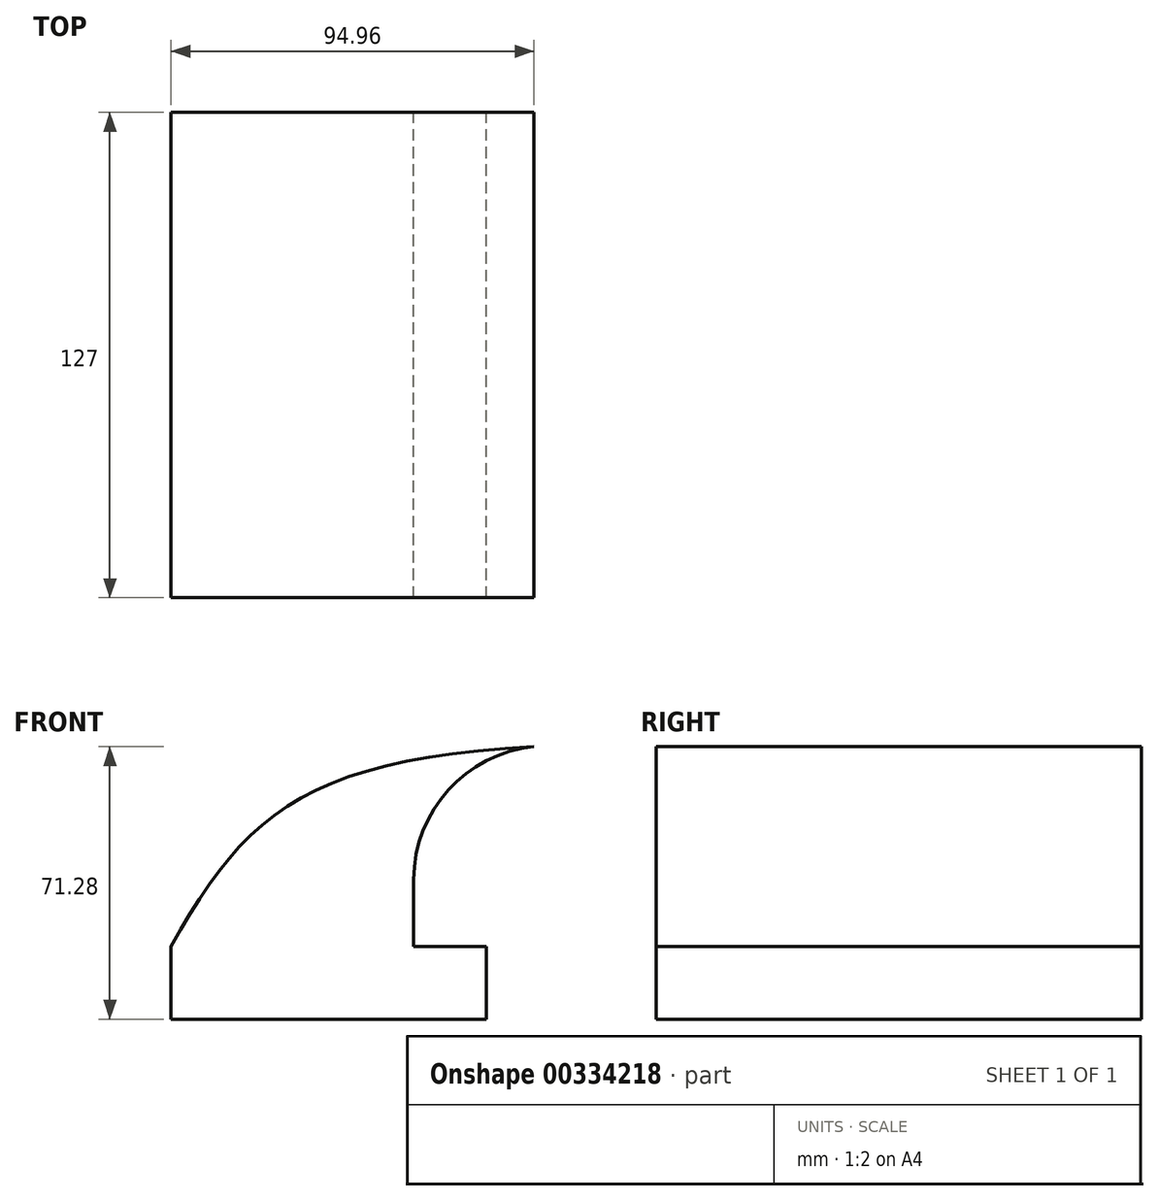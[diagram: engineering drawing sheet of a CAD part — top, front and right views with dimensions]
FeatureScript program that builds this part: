
annotation { "Feature Type Name" : "Feature", "Feature Type Description" : "" }
export const myFeature = defineFeature(function(context is Context, id is Id, definition is map)
    precondition{}
    {
        {
            var Q0;
            Q0=qCreatedBy(makeId("Front.planeOp"),FACE);
            var sketch = newSketch(context, id + "F0", { "sketchPlane" : qUnion([Q0])});
            skLineSegment(sketch, "E0.bottom", {"start": v(-41.28, 9.52) * mm, "end": v(41.28, 9.53) * mm});
            skLineSegment(sketch, "E0.top", {"start": v(-41.28, -9.52) * mm, "end": v(41.28, -9.52) * mm});
            skLineSegment(sketch, "E0.left", {"start": v(-41.28, 9.52) * mm, "end": v(-41.27, -9.53) * mm});
            skLineSegment(sketch, "E0.right", {"start": v(41.28, 9.53) * mm, "end": v(41.28, -9.52) * mm});
            skPoint(sketch, "E0.middle", {"position": v(0, 0) * mm});
            skLineSegment(sketch, "E1.bottom", {"start": v(130.2, 38.1) * mm, "end": v(79.4, 38.1) * mm});
            skLineSegment(sketch, "E1.top", {"start": v(130.2, 66.68) * mm, "end": v(79.4, 66.68) * mm});
            skLineSegment(sketch, "E1.left", {"start": v(130.2, 38.1) * mm, "end": v(130.2, 66.68) * mm});
            skLineSegment(sketch, "E1.right", {"start": v(79.4, 38.1) * mm, "end": v(79.4, 66.68) * mm});
            skPoint(sketch, "E1.middle", {"position": v(104.8, 52.39) * mm});
            skLineSegment(sketch, "E2", {"start": v(41.27, 9.53) * mm, "end": v(41.27, 27) * mm});
            skArc(sketch, "E3", {"start": v(41.27, 27) * mm, "mid": v(45.92, 38.23) * mm, "end": v(57.15, 42.88) * mm});
            skLineSegment(sketch, "E4", {"start": v(57.15, 42.88) * mm, "end": v(104.8, 42.88) * mm});
            skLineSegment(sketch, "E5.0", {"start": v(57.15, 61.93) * mm, "end": v(104.8, 61.93) * mm});
            skArc(sketch, "E5.1", {"start": v(22.22, 27) * mm, "mid": v(32.45, 51.7) * mm, "end": v(57.15, 61.93) * mm});
            skLineSegment(sketch, "E5.2", {"start": v(22.22, 9.53) * mm, "end": v(22.22, 27) * mm});
            skLineSegment(sketch, "E6", {"start": v(104.8, 38.1) * mm, "end": v(104.8, 66.68) * mm});
            skFitSpline(sketch, "E7", {"points": [v(-41.28, 9.52) * mm, v(57.15, 61.93) * mm], "startDerivative": vector(58.46, 104.75) * mm, "endDerivative": vector(188.23, 8.59) * mm});
            skSolve(sketch);
        }
        {
            var Q0;
            Q0=makeQuery(id+"F0.imprint","IMPRINT",FACE,{"disambiguationData":[TD([[makeQuery(id+"F0.imprint","IMPRINT",EDGE,{"derivedFrom":sQuery(id+"F0.wireOp",EDGE,"E0.top")}),1.0]])]});
            var Q1;
            {var subQ3=sQuery(id+"F0.wireOp",EDGE,"E5.2");Q1=makeQuery(id+"F0.imprint","IMPRINT",FACE,{"disambiguationData":[TD([[makeQuery(id+"F0.imprint","IMPRINT",EDGE,{"derivedFrom":subQ3}),1.0]])]});}
            extrude(context, id + "F1", {"entities" : qUnion([Q0, Q1]), "endBound" : BoundingType.SYMMETRIC, "depth" : 127 * mm});
        }
    });
